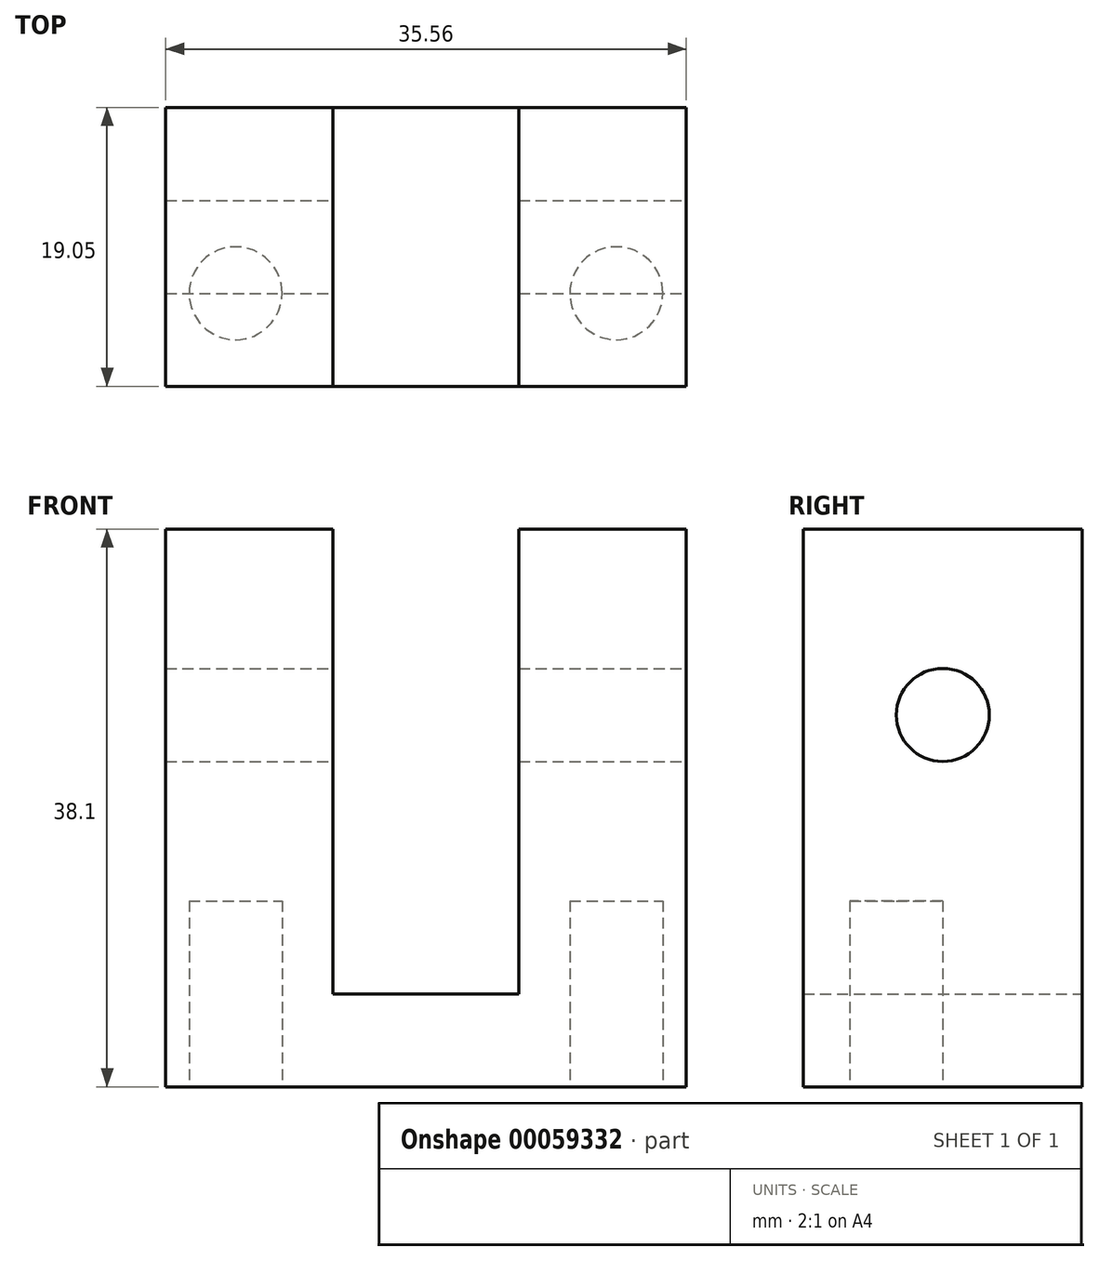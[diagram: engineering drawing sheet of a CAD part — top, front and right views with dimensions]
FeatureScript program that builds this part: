
annotation { "Feature Type Name" : "Feature", "Feature Type Description" : "" }
export const myFeature = defineFeature(function(context is Context, id is Id, definition is map)
    precondition{}
    {
        {
            var Q0;
            Q0=qCreatedBy(makeId("Front.planeOp"),FACE);
            var sketch = newSketch(context, id + "F0", { "sketchPlane" : qUnion([Q0])});
            skLineSegment(sketch, "E0", {"start": v(0, 0) * mm, "end": v(0, 38.1) * mm});
            skLineSegment(sketch, "E1", {"start": v(0, 38.1) * mm, "end": v(11.43, 38.1) * mm});
            skLineSegment(sketch, "E2", {"start": v(11.43, 38.1) * mm, "end": v(11.43, 6.35) * mm});
            skLineSegment(sketch, "E3", {"start": v(11.43, 6.35) * mm, "end": v(24.13, 6.35) * mm});
            skLineSegment(sketch, "E4", {"start": v(24.13, 6.35) * mm, "end": v(24.13, 38.1) * mm});
            skLineSegment(sketch, "E5", {"start": v(24.13, 38.1) * mm, "end": v(35.56, 38.1) * mm});
            skLineSegment(sketch, "E6", {"start": v(35.56, 38.1) * mm, "end": v(35.56, 0) * mm});
            skLineSegment(sketch, "E7", {"start": v(35.56, 0) * mm, "end": v(0, 0) * mm});
            skSolve(sketch);
        }
        {
            var Q0;
            Q0 = qSketchRegion(id + "F0", true);
            extrude(context, id + "F1", {"entities" : qUnion([Q0]), "depth" : 19.05 * mm});
        }
        {
            var Q0;
            Q0=makeQuery(id+"F1.opExtrude","SWEPT_FACE",FACE,{"disambiguationData":[OSD([sQuery(id+"F0.wireOp",EDGE,"E6")])]});
            var sketch = newSketch(context, id + "F2", { "sketchPlane" : qUnion([Q0])});
            skLineSegment(sketch, "E8", {"start": v(-9.53, -4.82) * mm, "end": v(-9.53, 44.83) * mm, "construction": true});
            skPoint(sketch, "E8.startSnap0", {"position": v(-9.53, 0) * mm});
            skCircle(sketch, "E9", {"center": v(-9.53, 25.4) * mm, "radius": 3.18 * mm});
            skSolve(sketch);
        }
        {
            var Q0;
            Q0 = qSketchRegion(id + "F2", true);
            extrude(context, id + "F3", {"entities" : qUnion([Q0]), "operationType" : NewBodyOperationType.REMOVE, "oppositeDirection" : true, "depth" : 53 * mm});
        }
        {
            var Q0;
            Q0=makeQuery(id+"F1.opExtrude","SWEPT_FACE",FACE,{"disambiguationData":[OSD([sQuery(id+"F0.wireOp",EDGE,"E7")])]});
            var sketch = newSketch(context, id + "F4", { "sketchPlane" : qUnion([Q0])});
            skCircle(sketch, "E10", {"center": v(4.78, 12.7) * mm, "radius": 3.18 * mm});
            skCircle(sketch, "E11", {"center": v(30.78, 12.7) * mm, "radius": 3.18 * mm});
            skSolve(sketch);
        }
        {
            var Q0;
            Q0 = qSketchRegion(id + "F4", true);
            extrude(context, id + "F5", {"entities" : qUnion([Q0]), "operationType" : NewBodyOperationType.REMOVE, "oppositeDirection" : true, "depth" : 12.7 * mm});
        }
    });
